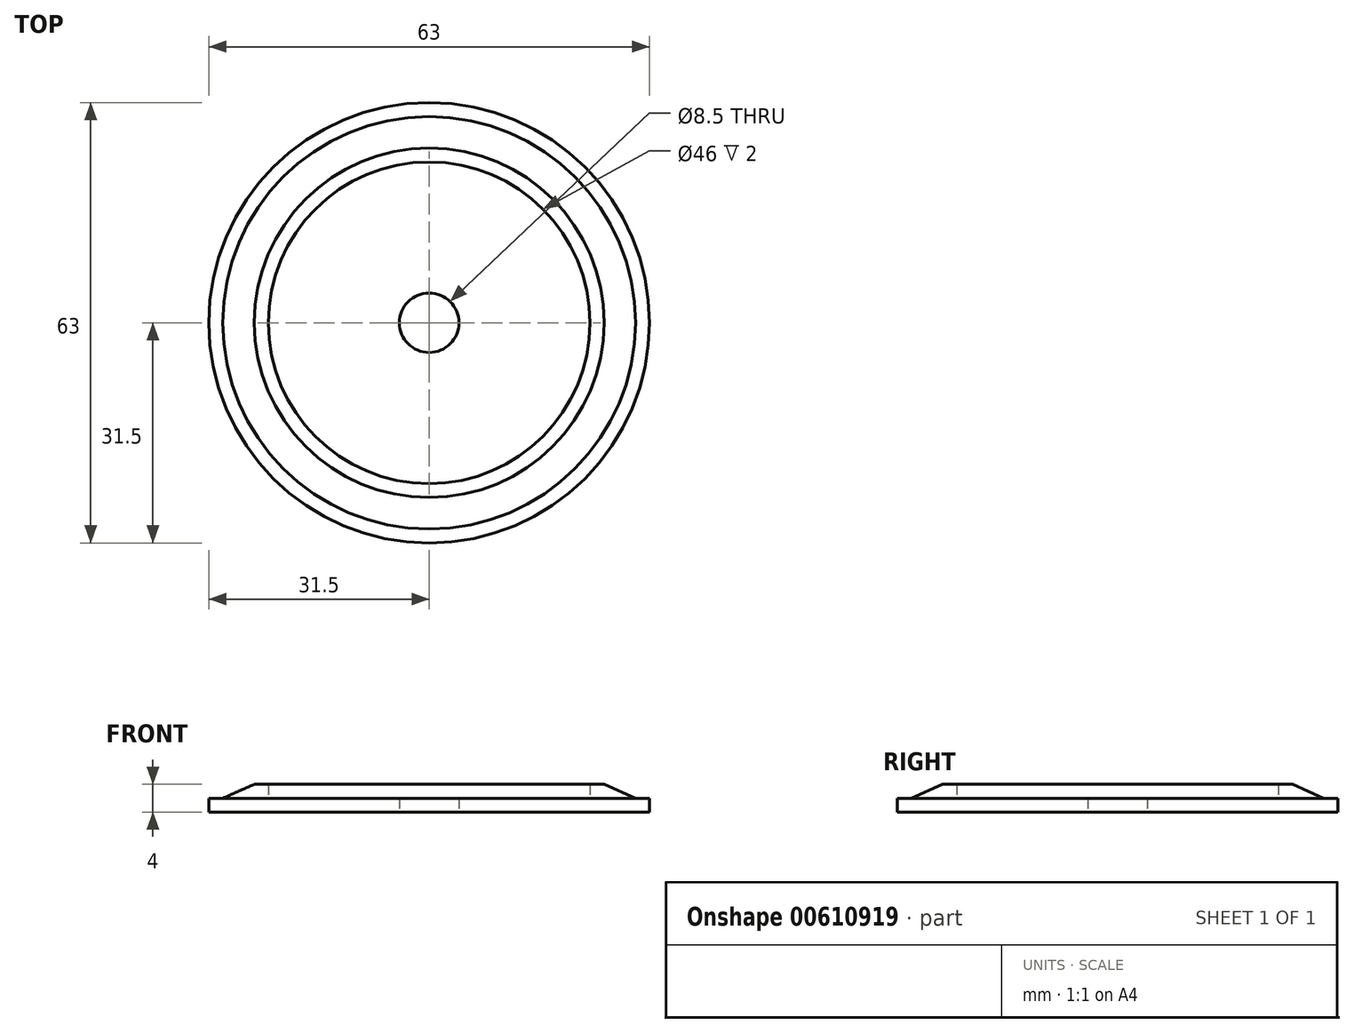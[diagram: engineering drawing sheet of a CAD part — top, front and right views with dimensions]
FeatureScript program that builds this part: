
annotation { "Feature Type Name" : "Feature", "Feature Type Description" : "" }
export const myFeature = defineFeature(function(context is Context, id is Id, definition is map)
    precondition{}
    {
        {
            var Q0;
            Q0=qCreatedBy(makeId("Front.planeOp"),FACE);
            var sketch = newSketch(context, id + "F0", { "sketchPlane" : qUnion([Q0])});
            skLineSegment(sketch, "E0", {"start": v(-4.25, 0) * mm, "end": v(-31.5, 0) * mm});
            skLineSegment(sketch, "E1", {"start": v(-31.5, 0) * mm, "end": v(-31.5, 2) * mm});
            skLineSegment(sketch, "E2", {"start": v(-31.5, 2) * mm, "end": v(-29.5, 2) * mm});
            skLineSegment(sketch, "E3", {"start": v(-29.5, 2) * mm, "end": v(-25, 4) * mm});
            skLineSegment(sketch, "E4", {"start": v(-25, 4) * mm, "end": v(-23, 4) * mm});
            skLineSegment(sketch, "E5", {"start": v(-23, 4) * mm, "end": v(-23, 2) * mm});
            skLineSegment(sketch, "E6", {"start": v(-23, 2) * mm, "end": v(-4.25, 2) * mm});
            skLineSegment(sketch, "E7", {"start": v(-4.25, 2) * mm, "end": v(-4.25, 0) * mm});
            skLineSegment(sketch, "E8", {"start": v(0, 0) * mm, "end": v(0, 60.55) * mm});
            skSolve(sketch);
        }
        {
            var Q0;
            Q0=makeQuery(id+"F0.imprint","IMPRINT",FACE,{"disambiguationData":[TD([[makeQuery(id+"F0.imprint","IMPRINT",EDGE,{"derivedFrom":sQuery(id+"F0.wireOp",EDGE,"E0")}),-1.0]])]});
            var Q1;
            Q1=sQuery(id+"F0.wireOp",EDGE,"E8");
            revolve(context, id + "F1", {"entities" : qUnion([Q0]), "axis" : qUnion([Q1]), "revolveType" : RevolveType.FULL});
        }
    });
